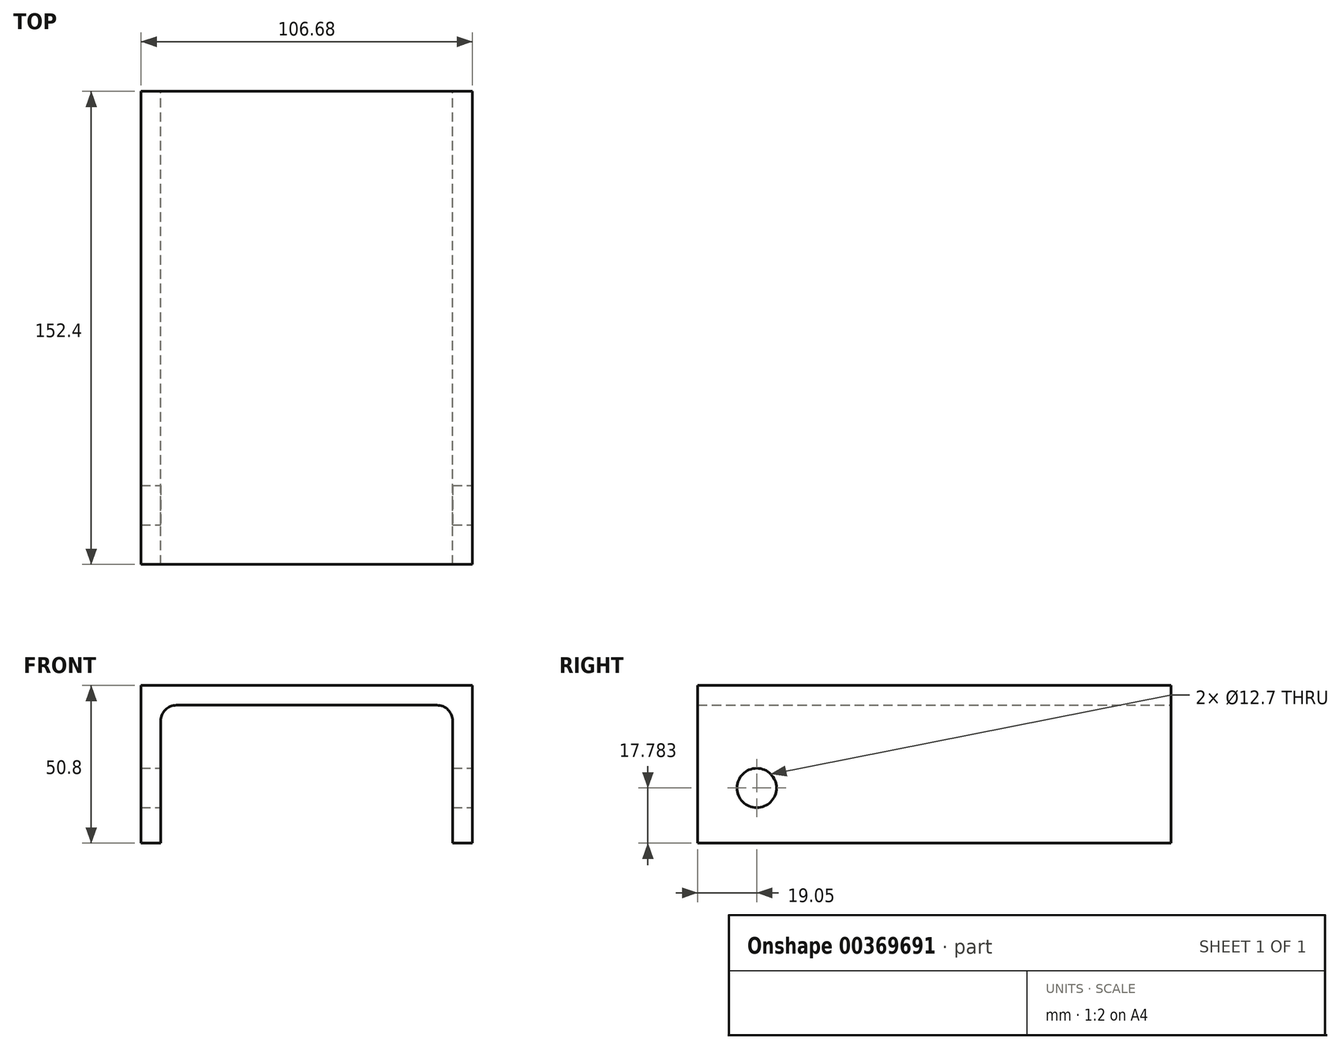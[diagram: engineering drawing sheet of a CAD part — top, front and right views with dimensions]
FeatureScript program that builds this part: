
annotation { "Feature Type Name" : "Feature", "Feature Type Description" : "" }
export const myFeature = defineFeature(function(context is Context, id is Id, definition is map)
    precondition{}
    {
        {
            var Q0;
            Q0=qCreatedBy(makeId("Front.planeOp"),FACE);
            var sketch = newSketch(context, id + "F0", { "sketchPlane" : qUnion([Q0])});
            skLineSegment(sketch, "E0.bottom", {"start": v(-47, 40.21) * mm, "end": v(47, 40.21) * mm});
            skLineSegment(sketch, "E0.left", {"start": v(-47, 40.21) * mm, "end": v(-47, -4.24) * mm});
            skLineSegment(sketch, "E0.right", {"start": v(47, 40.21) * mm, "end": v(47, -4.24) * mm});
            skLineSegment(sketch, "E1.1", {"start": v(-53.34, 46.56) * mm, "end": v(-53.34, -4.24) * mm});
            skLineSegment(sketch, "E1.2", {"start": v(-53.34, 46.56) * mm, "end": v(53.34, 46.56) * mm});
            skLineSegment(sketch, "E1.3", {"start": v(53.34, 46.56) * mm, "end": v(53.34, -4.24) * mm});
            skLineSegment(sketch, "E2", {"start": v(-53.34, -4.24) * mm, "end": v(-47, -4.24) * mm});
            skLineSegment(sketch, "E3.trimOffspring", {"start": v(46.99, -4.24) * mm, "end": v(53.34, -4.24) * mm});
            skSolve(sketch);
        }
        {
            var Q0;
            Q0 = qSketchRegion(id + "F0", true);
            extrude(context, id + "F1", {"entities" : qUnion([Q0]), "depth" : 152.4 * mm, "offsetDistance" : 25.4 * mm});
        }
        {
            var Q0;
            Q0=makeQuery(id+"F1.opExtrude","SWEPT_EDGE",EDGE,{"disambiguationData":[OSD([sQuery(id+"F0.wireOp",EDGE,"E0.bottom"),sQuery(id+"F0.wireOp",EDGE,"E0.left")])]});
            var Q1;
            Q1=makeQuery(id+"F1.opExtrude","SWEPT_EDGE",EDGE,{"disambiguationData":[OSD([sQuery(id+"F0.wireOp",EDGE,"E0.bottom"),sQuery(id+"F0.wireOp",EDGE,"E0.right")])]});
            fillet(context, id + "F2", {"entities" : qUnion([Q0, Q1]), "radius" : 5.08 * mm, "tangentPropagation" : true, "allowEdgeOverflow" : false});
        }
        {
            var Q0;
            Q0=makeQuery(id+"F1.opExtrude","SWEPT_FACE",FACE,{"disambiguationData":[OSD([sQuery(id+"F0.wireOp",EDGE,"E1.3")])]});
            var sketch = newSketch(context, id + "F3", { "sketchPlane" : qUnion([Q0])});
            skCircle(sketch, "E4", {"center": v(-133.35, 13.54) * mm, "radius": 6.35 * mm});
            skLineSegment(sketch, "E5", {"start": v(-152.4, 46.56) * mm, "end": v(-152.4, -4.24) * mm, "construction": true});
            skSolve(sketch);
        }
        {
            var Q0;
            Q0 = qSketchRegion(id + "F3", true);
            extrude(context, id + "F4", {"entities" : qUnion([Q0]), "operationType" : NewBodyOperationType.REMOVE, "endBound" : BoundingType.THROUGH_ALL, "oppositeDirection" : true, "depth" : 25.4 * mm, "offsetDistance" : 25.4 * mm});
        }
    });
